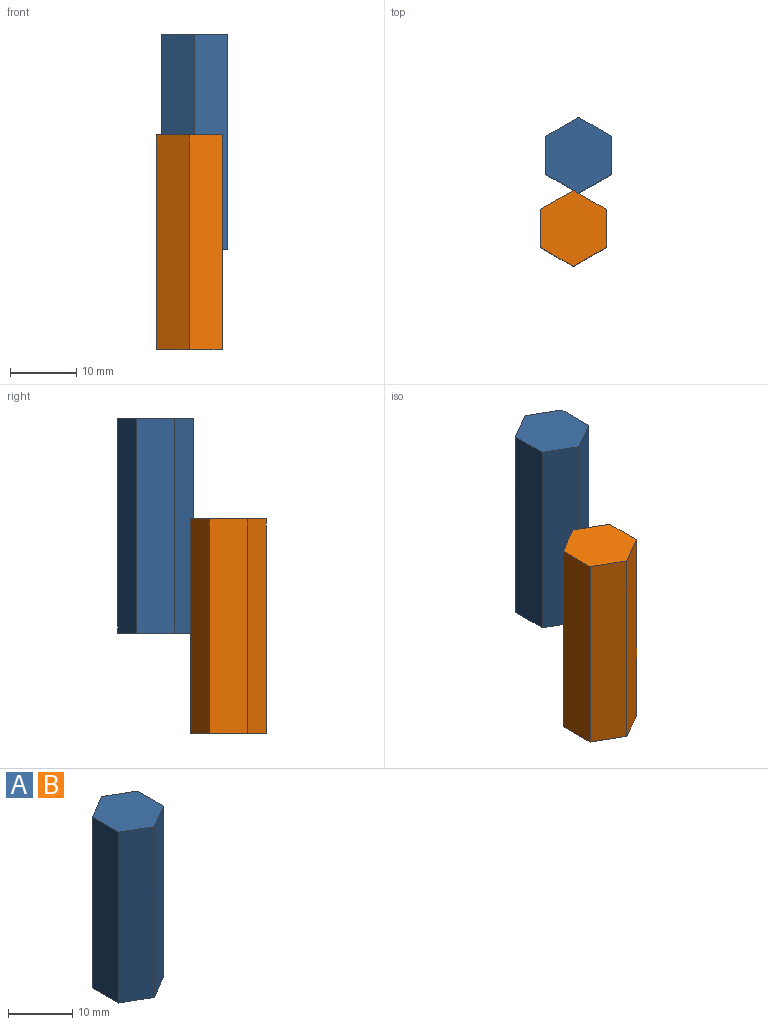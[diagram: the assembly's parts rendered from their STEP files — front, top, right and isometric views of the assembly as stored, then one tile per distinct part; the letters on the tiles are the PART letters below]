
ASSEMBLY  parts=2 mates=1
PART A: 8 faces, bbox 10x11.5x32.5 mm
  f0: plane 32.5x4.98mm, normal (0.5,0.87,0), area 186.9mm2, adj f1,f5,f6,f7
  f1: plane 32.5x4.98mm, normal (-0.5,0.87,0), area 186.9mm2, adj f0,f2,f6,f7
  f2: plane 32.5x5.75mm, normal (-1,0,0), area 186.9mm2, adj f1,f3,f6,f7
  f3: plane 32.5x4.98mm, normal (-0.5,-0.87,0), area 186.9mm2, adj f2,f4,f6,f7
  f4: plane 32.5x4.98mm, normal (0.5,-0.87,0), area 186.9mm2, adj f3,f5,f6,f7
  f5: plane 32.5x5.75mm, normal (1,0,0), area 186.9mm2, adj f0,f4,f6,f7
  f6: plane 11.5x9.96mm, normal (0,0,1), area 85.9mm2, adj f0,f1,f2,f3,f4,f5
  f7: plane 11.5x9.96mm, normal (0,0,-1), area 85.9mm2, adj f0,f1,f2,f3,f4,f5
PART B: same geometry as A
PLACE A rot(axis=(0.87,0.5,0),180deg) t=(-32.96,-21.14,18.13)mm
PLACE B rot(axis=(0,0,-1),180deg) t=(-33.77,-32.17,2.89)mm
MATE parallel A.f2 <-> B.f3  axis (-0.5,-0.87,0) through (-35.45,-25.45,18.13)mm
